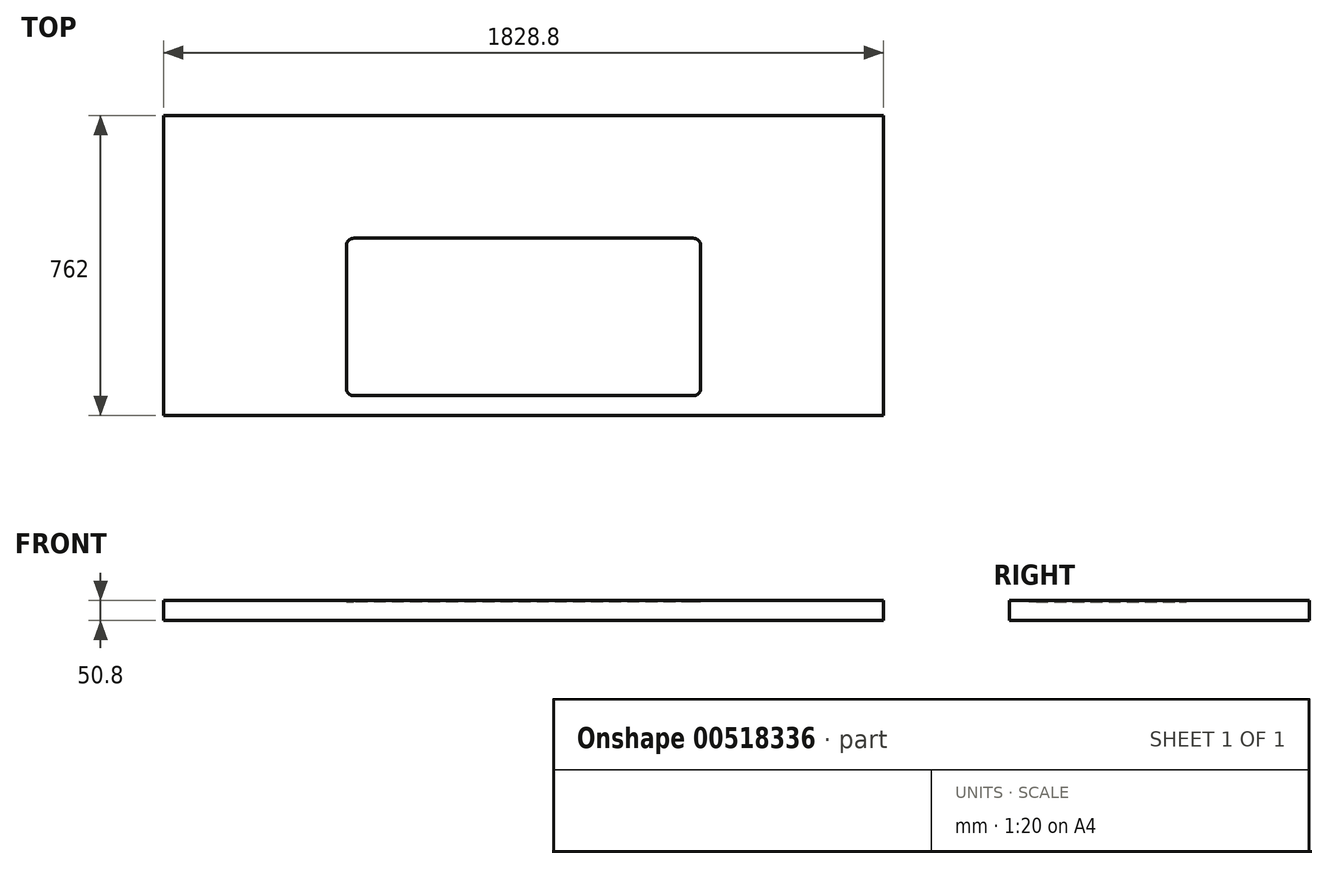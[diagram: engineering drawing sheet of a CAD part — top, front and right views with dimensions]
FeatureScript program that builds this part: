
annotation { "Feature Type Name" : "Feature", "Feature Type Description" : "" }
export const myFeature = defineFeature(function(context is Context, id is Id, definition is map)
    precondition{}
    {
        {
            var Q0;
            Q0=qCreatedBy(makeId("Top.planeOp"),FACE);
            var sketch = newSketch(context, id + "F0", { "sketchPlane" : qUnion([Q0])});
            skLineSegment(sketch, "E0.bottom", {"start": v(-914.4, 381) * mm, "end": v(914.4, 381) * mm});
            skLineSegment(sketch, "E0.top", {"start": v(-914.4, -381) * mm, "end": v(914.4, -381) * mm});
            skLineSegment(sketch, "E0.left", {"start": v(-914.4, 381) * mm, "end": v(-914.4, -381) * mm});
            skLineSegment(sketch, "E0.right", {"start": v(914.4, 381) * mm, "end": v(914.4, -381) * mm});
            skPoint(sketch, "E0.middle", {"position": v(0, 0) * mm});
            skSolve(sketch);
        }
        {
            var Q0;
            Q0=makeQuery(id+"F0.imprint","IMPRINT",FACE,{"disambiguationData":[TD([[makeQuery(id+"F0.imprint","IMPRINT",EDGE,{"derivedFrom":sQuery(id+"F0.wireOp",EDGE,"E0.bottom")}),-1.0]])]});
            extrude(context, id + "F1", {"entities" : qUnion([Q0]), "depth" : 50.8 * mm, "offsetDistance" : 25.4 * mm});
        }
        {
            var Q0;
            Q0=makeQuery(id+"F1.opExtrude","CAP_FACE",FACE,{"disambiguationData":[OSD([sQuery(id+"F0.wireOp",EDGE,"E0.bottom"),sQuery(id+"F0.wireOp",EDGE,"E0.top"),sQuery(id+"F0.wireOp",EDGE,"E0.left"),sQuery(id+"F0.wireOp",EDGE,"E0.right")])],"isStart":false});
            var sketch = newSketch(context, id + "F2", { "sketchPlane" : qUnion([Q0])});
            skLineSegment(sketch, "E1.bottom", {"start": v(431.74, -330.91) * mm, "end": v(-431.74, -330.91) * mm});
            skLineSegment(sketch, "E1.top", {"start": v(431.74, 69.09) * mm, "end": v(-431.73, 69.09) * mm});
            skLineSegment(sketch, "E1.left", {"start": v(450, -312.65) * mm, "end": v(450, 50.83) * mm});
            skLineSegment(sketch, "E1.right", {"start": v(-450, -312.65) * mm, "end": v(-450, 50.82) * mm});
            skPoint(sketch, "E1.middle", {"position": v(0, -130.91) * mm});
            skPoint(sketch, "E2.visualSharp", {"position": v(-450, 69.09) * mm});
            skArc(sketch, "E2.filletArc", {"start": v(-431.73, 69.09) * mm, "mid": v(-444.65, 63.74) * mm, "end": v(-450, 50.82) * mm});
            skPoint(sketch, "E3.visualSharp", {"position": v(450, 69.09) * mm});
            skArc(sketch, "E3.filletArc", {"start": v(450, 50.83) * mm, "mid": v(444.65, 63.74) * mm, "end": v(431.74, 69.09) * mm});
            skPoint(sketch, "E4.visualSharp", {"position": v(450, -330.91) * mm});
            skArc(sketch, "E4.filletArc", {"start": v(431.74, -330.91) * mm, "mid": v(444.65, -325.56) * mm, "end": v(450, -312.65) * mm});
            skPoint(sketch, "E5.visualSharp", {"position": v(-450, -330.91) * mm});
            skArc(sketch, "E5.filletArc", {"start": v(-450, -312.65) * mm, "mid": v(-444.65, -325.56) * mm, "end": v(-431.74, -330.91) * mm});
            skSolve(sketch);
        }
        {
            var Q0;
            Q0=makeQuery(id+"F2.imprint","IMPRINT",FACE,{"disambiguationData":[TD([[makeQuery(id+"F2.imprint","IMPRINT",EDGE,{"derivedFrom":sQuery(id+"F2.wireOp",EDGE,"E1.bottom")}),-1.0]])]});
            extrude(context, id + "F3", {"entities" : qUnion([Q0]), "operationType" : NewBodyOperationType.REMOVE, "oppositeDirection" : true, "depth" : 4 * mm});
        }
    });
